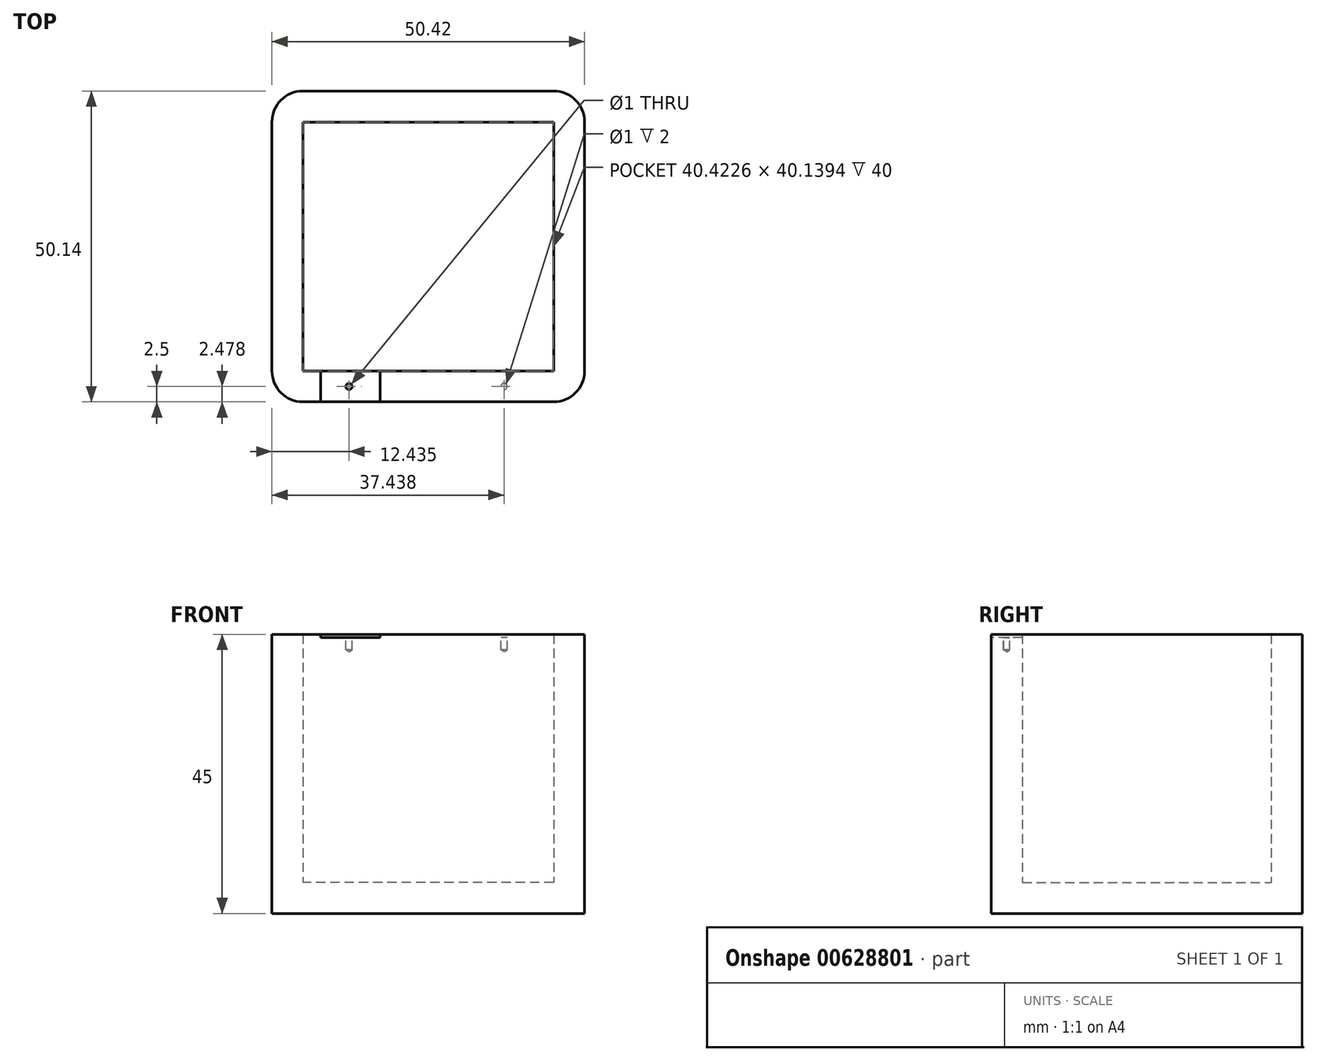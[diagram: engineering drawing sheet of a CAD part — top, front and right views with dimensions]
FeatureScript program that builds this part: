
annotation { "Feature Type Name" : "Feature", "Feature Type Description" : "" }
export const myFeature = defineFeature(function(context is Context, id is Id, definition is map)
    precondition{}
    {
        {
            var Q0;
            Q0=qCreatedBy(makeId("Top.planeOp"),FACE);
            var sketch = newSketch(context, id + "F0", { "sketchPlane" : qUnion([Q0])});
            skLineSegment(sketch, "E0.bottom", {"start": v(25.21, -25.07) * mm, "end": v(-25.21, -25.07) * mm});
            skLineSegment(sketch, "E0.top", {"start": v(25.21, 25.07) * mm, "end": v(-25.21, 25.07) * mm});
            skLineSegment(sketch, "E0.left", {"start": v(25.21, -25.07) * mm, "end": v(25.21, 25.07) * mm});
            skLineSegment(sketch, "E0.right", {"start": v(-25.21, -25.07) * mm, "end": v(-25.21, 25.07) * mm});
            skPoint(sketch, "E0.middle", {"position": v(0, 0) * mm});
            skSolve(sketch);
        }
        {
            var Q0;
            Q0=makeQuery(id+"F0.imprint","IMPRINT",FACE,{"disambiguationData":[TD([[makeQuery(id+"F0.imprint","IMPRINT",EDGE,{"derivedFrom":sQuery(id+"F0.wireOp",EDGE,"E0.bottom")}),-1.0]])]});
            extrude(context, id + "F1", {"entities" : qUnion([Q0]), "depth" : 45 * mm, "offsetDistance" : 25 * mm});
        }
        {
            var Q0;
            Q0=makeQuery(id+"F1.opExtrude","CAP_FACE",FACE,{"disambiguationData":[OSD([sQuery(id+"F0.wireOp",EDGE,"E0.bottom"),sQuery(id+"F0.wireOp",EDGE,"E0.top"),sQuery(id+"F0.wireOp",EDGE,"E0.left"),sQuery(id+"F0.wireOp",EDGE,"E0.right")])],"isStart":false});
            shell(context, id + "F2", {"entities" : qUnion([Q0]), "thickness" : 5 * mm});
        }
        {
            var Q0;
            Q0=makeQuery(id+"F1.opExtrude","CAP_FACE",FACE,{"disambiguationData":[OSD([sQuery(id+"F0.wireOp",EDGE,"E0.bottom"),sQuery(id+"F0.wireOp",EDGE,"E0.top"),sQuery(id+"F0.wireOp",EDGE,"E0.left"),sQuery(id+"F0.wireOp",EDGE,"E0.right")])],"isStart":false});
            var sketch = newSketch(context, id + "F3", { "sketchPlane" : qUnion([Q0])});
            skLineSegment(sketch, "E1.bottom", {"start": v(-17.34, -20.07) * mm, "end": v(-7.74, -20.07) * mm});
            skLineSegment(sketch, "E1.top", {"start": v(-17.34, -25.07) * mm, "end": v(-7.74, -25.07) * mm});
            skLineSegment(sketch, "E1.left", {"start": v(-17.34, -20.07) * mm, "end": v(-17.34, -25.07) * mm});
            skLineSegment(sketch, "E1.right", {"start": v(-7.74, -20.07) * mm, "end": v(-7.74, -25.07) * mm});
            skSolve(sketch);
        }
        {
            var Q0;
            Q0 = qSketchRegion(id + "F3", true);
            extrude(context, id + "F4", {"entities" : qUnion([Q0]), "operationType" : NewBodyOperationType.REMOVE, "oppositeDirection" : true, "depth" : .5 * mm, "offsetDistance" : 25 * mm});
        }
        {
            var Q0;
            Q0=makeQuery(id+"F4.boolean.opBoolean","COPY",FACE,{"derivedFrom":makeQuery(id+"F4.opExtrude","CAP_FACE",FACE,{"disambiguationData":[OSD([sQuery(id+"F3.wireOp",EDGE,"E1.bottom"),sQuery(id+"F3.wireOp",EDGE,"E1.top"),sQuery(id+"F3.wireOp",EDGE,"E1.left"),sQuery(id+"F3.wireOp",EDGE,"E1.right")])],"isStart":false})});
            var sketch = newSketch(context, id + "F5", { "sketchPlane" : qUnion([Q0])});
            skPoint(sketch, "E2", {"position": v(-12.78, -22.6) * mm});
            skPoint(sketch, "E3", {"position": v(12.23, -22.57) * mm});
            skPoint(sketch, "E3.positionSnap0", {"position": v(-17.34, -22.57) * mm});
            skSolve(sketch);
        }
        {
            var Q0;
            Q0=sQuery(id+"F5.wireOp",VERTEX,"E2");
            var Q1;
            Q1=sQuery(id+"F5.wireOp",VERTEX,"E3");
            var Q2;
            Q2=makeQuery(id+"F1.opExtrude","SWEPT_BODY",BODY,{"disambiguationData":[OSD([sQuery(id+"F0.wireOp",EDGE,"E0.bottom"),sQuery(id+"F0.wireOp",EDGE,"E0.top"),sQuery(id+"F0.wireOp",EDGE,"E0.left"),sQuery(id+"F0.wireOp",EDGE,"E0.right")])]});
            hole(context, id + "F6", {"style" : HoleStyle.SIMPLE, "endStyle" : HoleEndStyle.BLIND, "holeDiameter" : 1 * mm, "majorDiameter" : 5 * mm, "holeDepth" : 2 * mm, "isTappedThrough" : true, "tappedDepth" : 12 * mm, "tapClearance" : 3, "locations" : qUnion([Q0, Q1]), "scope" : qUnion([Q2])});
        }
        {
            var Q0;
            Q0=makeQuery(id+"F1.opExtrude","SWEPT_EDGE",EDGE,{"disambiguationData":[OSD([sQuery(id+"F0.wireOp",EDGE,"E0.bottom"),sQuery(id+"F0.wireOp",EDGE,"E0.left")])]});
            var Q1;
            Q1=makeQuery(id+"F1.opExtrude","SWEPT_EDGE",EDGE,{"disambiguationData":[OSD([sQuery(id+"F0.wireOp",EDGE,"E0.bottom"),sQuery(id+"F0.wireOp",EDGE,"E0.right")])]});
            var Q2;
            Q2=makeQuery(id+"F1.opExtrude","SWEPT_EDGE",EDGE,{"disambiguationData":[OSD([sQuery(id+"F0.wireOp",EDGE,"E0.top"),sQuery(id+"F0.wireOp",EDGE,"E0.right")])]});
            var Q3;
            Q3=makeQuery(id+"F1.opExtrude","SWEPT_EDGE",EDGE,{"disambiguationData":[OSD([sQuery(id+"F0.wireOp",EDGE,"E0.top"),sQuery(id+"F0.wireOp",EDGE,"E0.left")])]});
            fillet(context, id + "F7", {"entities" : qUnion([Q0, Q1, Q2, Q3]), "radius" : 5 * mm, "tangentPropagation" : true, "allowEdgeOverflow" : false});
        }
    });
